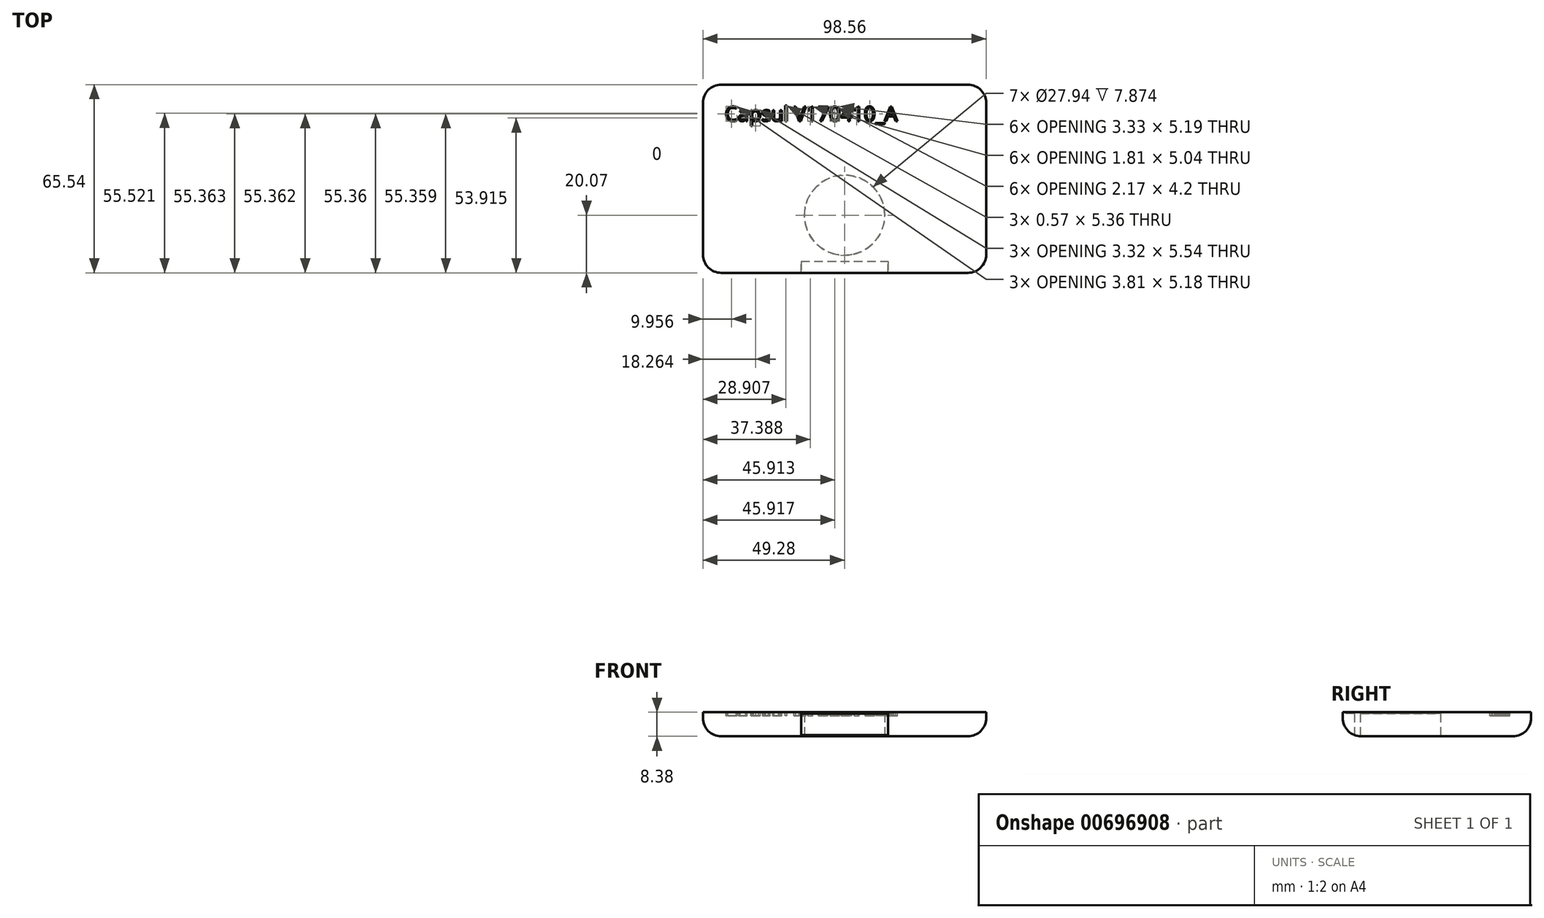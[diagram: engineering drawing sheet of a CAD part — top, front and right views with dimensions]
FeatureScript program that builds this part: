
annotation { "Feature Type Name" : "Feature", "Feature Type Description" : "" }
export const myFeature = defineFeature(function(context is Context, id is Id, definition is map)
    precondition{}
    {
        {
            var Q0;
            Q0=qCreatedBy(makeId("Top.planeOp"),FACE);
            var sketch = newSketch(context, id + "F0", { "sketchPlane" : qUnion([Q0])});
            skLineSegment(sketch, "E0.bottom", {"start": v(49.28, 32.77) * mm, "end": v(-49.28, 32.77) * mm});
            skLineSegment(sketch, "E0.top", {"start": v(49.28, -32.77) * mm, "end": v(-49.28, -32.77) * mm});
            skLineSegment(sketch, "E0.left", {"start": v(49.28, 32.77) * mm, "end": v(49.28, -32.77) * mm});
            skLineSegment(sketch, "E0.right", {"start": v(-49.28, 32.77) * mm, "end": v(-49.28, -32.77) * mm});
            skPoint(sketch, "E0.middle", {"position": v(0, 0) * mm});
            skSolve(sketch);
        }
        {
            var Q0;
            Q0=makeQuery(id+"F0.imprint","IMPRINT",FACE,{"disambiguationData":[TD([[makeQuery(id+"F0.imprint","IMPRINT",EDGE,{"derivedFrom":sQuery(id+"F0.wireOp",EDGE,"E0.bottom")}),1.0]])]});
            extrude(context, id + "F1", {"entities" : qUnion([Q0]), "depth" : 8.38 * mm, "offsetDistance" : 25.4 * mm});
        }
        {
            var Q0;
            Q0=makeQuery(id+"F1.opExtrude","SWEPT_EDGE",EDGE,{"disambiguationData":[OSD([sQuery(id+"F0.wireOp",EDGE,"E0.top"),sQuery(id+"F0.wireOp",EDGE,"E0.right")])]});
            var Q1;
            Q1=makeQuery(id+"F1.opExtrude","SWEPT_EDGE",EDGE,{"disambiguationData":[OSD([sQuery(id+"F0.wireOp",EDGE,"E0.top"),sQuery(id+"F0.wireOp",EDGE,"E0.left")])]});
            var Q2;
            Q2=makeQuery(id+"F1.opExtrude","SWEPT_EDGE",EDGE,{"disambiguationData":[OSD([sQuery(id+"F0.wireOp",EDGE,"E0.bottom"),sQuery(id+"F0.wireOp",EDGE,"E0.left")])]});
            var Q3;
            Q3=makeQuery(id+"F1.opExtrude","SWEPT_EDGE",EDGE,{"disambiguationData":[OSD([sQuery(id+"F0.wireOp",EDGE,"E0.bottom"),sQuery(id+"F0.wireOp",EDGE,"E0.right")])]});
            var Q4;
            Q4=makeQuery(id+"F1.opExtrude","CAP_FACE",FACE,{"disambiguationData":[OSD([sQuery(id+"F0.wireOp",EDGE,"E0.bottom"),sQuery(id+"F0.wireOp",EDGE,"E0.top"),sQuery(id+"F0.wireOp",EDGE,"E0.left"),sQuery(id+"F0.wireOp",EDGE,"E0.right")])],"isStart":true});
            fillet(context, id + "F2", {"entities" : qUnion([Q0, Q1, Q2, Q3, Q4]), "radius" : 6.35 * mm, "tangentPropagation" : true, "allowEdgeOverflow" : false});
        }
        {
            var Q0;
            Q0=makeQuery(id+"F1.opExtrude","CAP_FACE",FACE,{"disambiguationData":[OSD([sQuery(id+"F0.wireOp",EDGE,"E0.bottom"),sQuery(id+"F0.wireOp",EDGE,"E0.top"),sQuery(id+"F0.wireOp",EDGE,"E0.left"),sQuery(id+"F0.wireOp",EDGE,"E0.right")])],"isStart":true});
            var sketch = newSketch(context, id + "F3", { "sketchPlane" : qUnion([Q0])});
            skCircle(sketch, "E1", {"center": v(0, 12.7) * mm, "radius": 13.97 * mm});
            skSolve(sketch);
        }
        {
            var Q0;
            Q0 = qSketchRegion(id + "F3", true);
            extrude(context, id + "F4", {"entities" : qUnion([Q0]), "operationType" : NewBodyOperationType.REMOVE, "oppositeDirection" : true, "depth" : 7.87 * mm, "offsetDistance" : 25.4 * mm});
        }
        {
            var Q0;
            Q0=qCreatedBy(makeId("Top.planeOp"),FACE);
            var sketch = newSketch(context, id + "F5", { "sketchPlane" : qUnion([Q0])});
            skLineSegment(sketch, "E2.bottom", {"start": v(15.15, -28.75) * mm, "end": v(-15.15, -28.75) * mm});
            skLineSegment(sketch, "E2.top", {"start": v(15.15, -37.3) * mm, "end": v(-15.15, -37.3) * mm});
            skLineSegment(sketch, "E2.left", {"start": v(15.15, -28.75) * mm, "end": v(15.15, -37.3) * mm});
            skLineSegment(sketch, "E2.right", {"start": v(-15.15, -28.75) * mm, "end": v(-15.15, -37.3) * mm});
            skPoint(sketch, "E2.middle", {"position": v(0, -33.03) * mm});
            skSolve(sketch);
        }
        {
            var Q0;
            Q0 = qSketchRegion(id + "F5", true);
            extrude(context, id + "F6", {"entities" : qUnion([Q0]), "operationType" : NewBodyOperationType.REMOVE, "depth" : 7.87 * mm, "offsetDistance" : 25.4 * mm});
        }
        {
            var Q0;
            Q0=makeQuery(id+"F1.opExtrude","CAP_FACE",FACE,{"disambiguationData":[OSD([sQuery(id+"F0.wireOp",EDGE,"E0.bottom"),sQuery(id+"F0.wireOp",EDGE,"E0.top"),sQuery(id+"F0.wireOp",EDGE,"E0.left"),sQuery(id+"F0.wireOp",EDGE,"E0.right")])],"isStart":false});
            var sketch = newSketch(context, id + "F7", { "sketchPlane" : qUnion([Q0])});
            skText(sketch, "E3", { "text": "Capsul V170410_A\n", "fontName": "OpenSans-Regular.ttf"});
            const initialGuessF7  = {"E3": [-0.04166, 0.02007, 1, 0, 0.00508]};
            skSetInitialGuess(sketch, initialGuessF7);
            skSolve(sketch);
        }
        {
            var Q0;
            Q0 = qSketchRegion(id + "F7", true);
            extrude(context, id + "F8", {"entities" : qUnion([Q0]), "operationType" : NewBodyOperationType.REMOVE, "oppositeDirection" : true, "depth" : 1.27 * mm, "offsetDistance" : 25.4 * mm});
        }
    });
